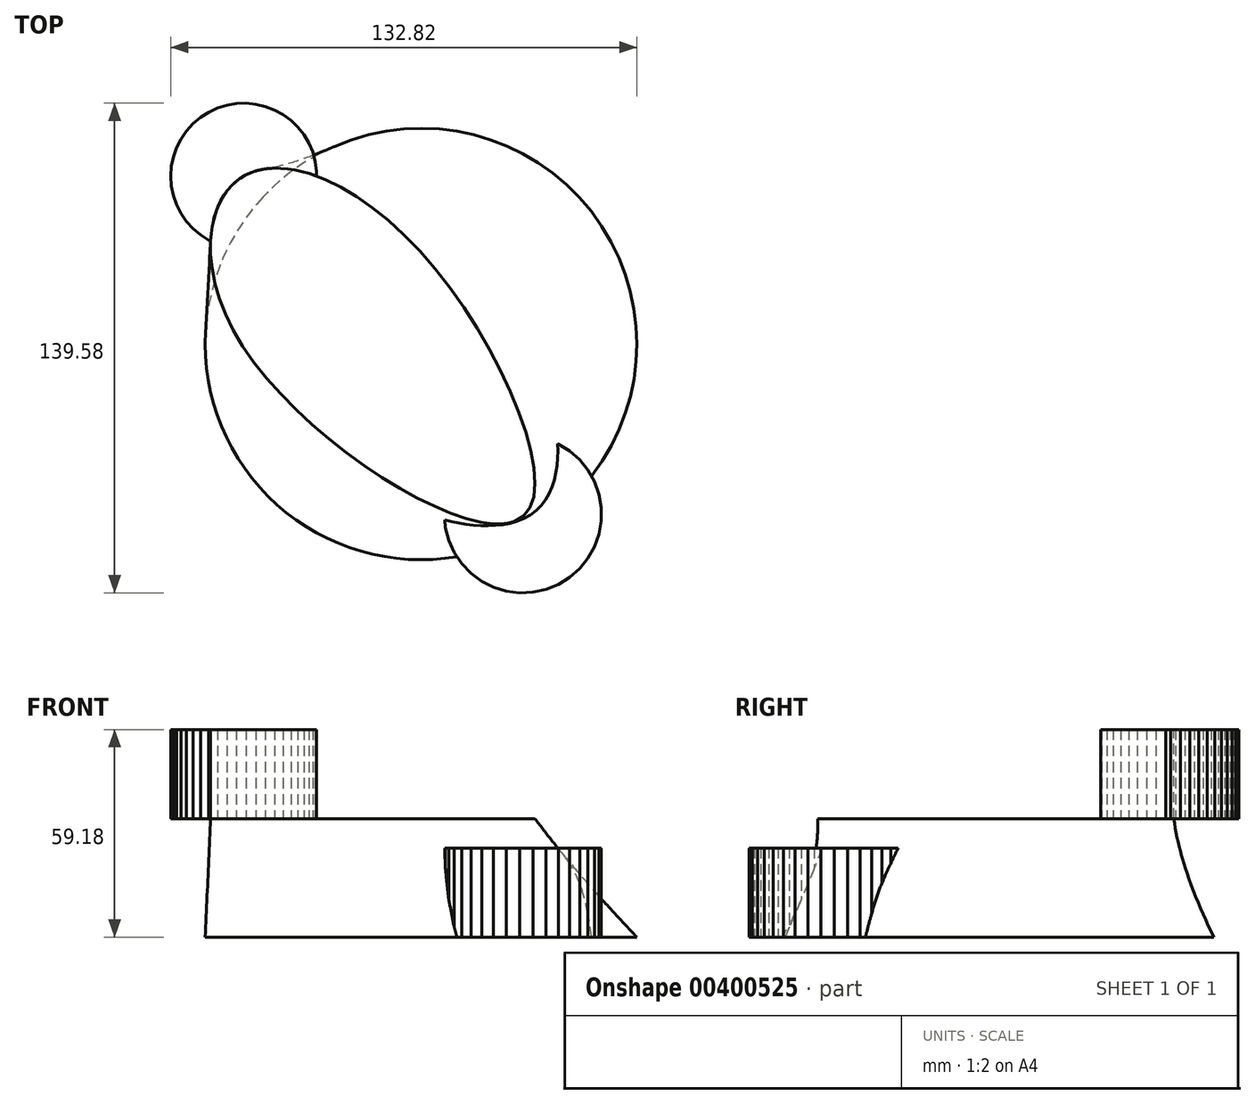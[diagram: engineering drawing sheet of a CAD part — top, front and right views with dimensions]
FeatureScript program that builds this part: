
annotation { "Feature Type Name" : "Feature", "Feature Type Description" : "" }
export const myFeature = defineFeature(function(context is Context, id is Id, definition is map)
    precondition{}
    {
        {
            var Q0;
            Q0=qCreatedBy(makeId("Top.planeOp"),FACE);
            cPlane(context, id + "F0", {"entities" : qUnion([Q0]), "cplaneType" : CPlaneType.OFFSET, "offset" : 33.78 * mm, "width" : 152.4 * mm, "height" : 152.4 * mm});
        }
        {
            var Q0;
            Q0=qCreatedBy(makeId("Top.planeOp"),FACE);
            var sketch = newSketch(context, id + "F1", { "sketchPlane" : qUnion([Q0])});
            skCircle(sketch, "E0", {"center": v(0, 0) * mm, "radius": 61.5 * mm});
            skSolve(sketch);
        }
        {
            var Q0;
            Q0=qCreatedBy(id+"F0.planeOp",FACE);
            var sketch = newSketch(context, id + "F2", { "sketchPlane" : qUnion([Q0])});
            skFitSpline(sketch, "E1", {"points": [v(-51.05, 47.53) * mm, v(0, 26.14) * mm, v(28.63, -49.58) * mm, v(-51.22, 0) * mm, v(-51.05, 47.53) * mm]});
            skSolve(sketch);
        }
        {
            var Q0;
            Q0 = qSketchRegion(id + "F2", true);
            var Q1;
            Q1 = qSketchRegion(id + "F1", true);
            loft(context, id + "F3", {"sheetProfilesArray" : [{ "sheetProfileEntities" : qUnion([Q0]) }, { "sheetProfileEntities" : qUnion([Q1]) }]});
        }
        {
            var Q0;
            Q0=makeQuery(id+"F3.opLoft","CAP_FACE",FACE,{"disambiguationData":[OSD([makeQuery(id+"F2.imprint","IMPRINT",FACE,{"disambiguationData":[TD([[makeQuery(id+"F2.imprint","IMPRINT",EDGE,{"derivedFrom":sQuery(id+"F2.wireOp",EDGE,"E1")}),-1.0]])]})])],"isStart":true});
            var sketch = newSketch(context, id + "F4", { "sketchPlane" : qUnion([Q0])});
            skCircle(sketch, "E2.cCircle", {"center": v(-50.5, 47.86) * mm, "radius": 20.76 * mm, "construction": true});
            skLineSegment(sketch, "E2.0", {"start": v(-29.74, 49.25) * mm, "end": v(-29.74, 46.47) * mm});
            skLineSegment(sketch, "E2.1", {"start": v(-29.74, 46.47) * mm, "end": v(-30.11, 43.71) * mm});
            skLineSegment(sketch, "E2.2", {"start": v(-30.11, 43.71) * mm, "end": v(-30.85, 41.03) * mm});
            skLineSegment(sketch, "E2.3", {"start": v(-30.85, 41.03) * mm, "end": v(-31.93, 38.47) * mm});
            skLineSegment(sketch, "E2.4", {"start": v(-31.93, 38.47) * mm, "end": v(-33.35, 36.08) * mm});
            skLineSegment(sketch, "E2.5", {"start": v(-33.35, 36.08) * mm, "end": v(-35.07, 33.9) * mm});
            skLineSegment(sketch, "E2.6", {"start": v(-35.07, 33.9) * mm, "end": v(-37.07, 31.97) * mm});
            skLineSegment(sketch, "E2.7", {"start": v(-37.07, 31.97) * mm, "end": v(-39.3, 30.32) * mm});
            skLineSegment(sketch, "E2.8", {"start": v(-39.3, 30.32) * mm, "end": v(-41.75, 28.98) * mm});
            skLineSegment(sketch, "E2.9", {"start": v(-41.75, 28.98) * mm, "end": v(-44.34, 27.98) * mm});
            skLineSegment(sketch, "E2.10", {"start": v(-44.34, 27.98) * mm, "end": v(-47.04, 27.34) * mm});
            skLineSegment(sketch, "E2.11", {"start": v(-47.04, 27.34) * mm, "end": v(-49.8, 27.06) * mm});
            skLineSegment(sketch, "E2.12", {"start": v(-49.8, 27.06) * mm, "end": v(-52.59, 27.15) * mm});
            skLineSegment(sketch, "E2.13", {"start": v(-52.59, 27.15) * mm, "end": v(-55.33, 27.62) * mm});
            skLineSegment(sketch, "E2.14", {"start": v(-55.33, 27.62) * mm, "end": v(-57.98, 28.44) * mm});
            skLineSegment(sketch, "E2.15", {"start": v(-57.98, 28.44) * mm, "end": v(-60.5, 29.6) * mm});
            skLineSegment(sketch, "E2.16", {"start": v(-60.5, 29.6) * mm, "end": v(-62.85, 31.1) * mm});
            skLineSegment(sketch, "E2.17", {"start": v(-62.85, 31.1) * mm, "end": v(-64.97, 32.9) * mm});
            skLineSegment(sketch, "E2.18", {"start": v(-64.97, 32.9) * mm, "end": v(-66.84, 34.96) * mm});
            skLineSegment(sketch, "E2.19", {"start": v(-66.84, 34.96) * mm, "end": v(-68.4, 37.25) * mm});
            skLineSegment(sketch, "E2.20", {"start": v(-68.4, 37.25) * mm, "end": v(-69.66, 39.73) * mm});
            skLineSegment(sketch, "E2.21", {"start": v(-69.66, 39.73) * mm, "end": v(-70.57, 42.36) * mm});
            skLineSegment(sketch, "E2.22", {"start": v(-70.57, 42.36) * mm, "end": v(-71.13, 45.08) * mm});
            skLineSegment(sketch, "E2.23", {"start": v(-71.13, 45.08) * mm, "end": v(-71.31, 47.86) * mm});
            skLineSegment(sketch, "E2.24", {"start": v(-71.31, 47.86) * mm, "end": v(-71.13, 50.63) * mm});
            skLineSegment(sketch, "E2.25", {"start": v(-71.13, 50.63) * mm, "end": v(-70.57, 53.35) * mm});
            skLineSegment(sketch, "E2.26", {"start": v(-70.57, 53.35) * mm, "end": v(-69.66, 55.98) * mm});
            skLineSegment(sketch, "E2.27", {"start": v(-69.66, 55.98) * mm, "end": v(-68.4, 58.46) * mm});
            skLineSegment(sketch, "E2.28", {"start": v(-68.4, 58.46) * mm, "end": v(-66.84, 60.75) * mm});
            skLineSegment(sketch, "E2.29", {"start": v(-66.84, 60.75) * mm, "end": v(-64.97, 62.81) * mm});
            skLineSegment(sketch, "E2.30", {"start": v(-64.97, 62.81) * mm, "end": v(-62.85, 64.6) * mm});
            skLineSegment(sketch, "E2.31", {"start": v(-62.85, 64.6) * mm, "end": v(-60.5, 66.1) * mm});
            skLineSegment(sketch, "E2.32", {"start": v(-60.5, 66.1) * mm, "end": v(-57.98, 67.28) * mm});
            skLineSegment(sketch, "E2.33", {"start": v(-57.98, 67.28) * mm, "end": v(-55.33, 68.1) * mm});
            skLineSegment(sketch, "E2.34", {"start": v(-55.33, 68.1) * mm, "end": v(-52.59, 68.56) * mm});
            skLineSegment(sketch, "E2.35", {"start": v(-52.59, 68.56) * mm, "end": v(-49.8, 68.65) * mm});
            skLineSegment(sketch, "E2.36", {"start": v(-49.8, 68.65) * mm, "end": v(-47.04, 68.38) * mm});
            skLineSegment(sketch, "E2.37", {"start": v(-47.04, 68.38) * mm, "end": v(-44.34, 67.73) * mm});
            skLineSegment(sketch, "E2.38", {"start": v(-44.34, 67.73) * mm, "end": v(-41.75, 66.73) * mm});
            skLineSegment(sketch, "E2.39", {"start": v(-41.75, 66.73) * mm, "end": v(-39.3, 65.4) * mm});
            skLineSegment(sketch, "E2.40", {"start": v(-39.3, 65.4) * mm, "end": v(-37.07, 63.75) * mm});
            skLineSegment(sketch, "E2.41", {"start": v(-37.07, 63.75) * mm, "end": v(-35.07, 61.82) * mm});
            skLineSegment(sketch, "E2.42", {"start": v(-35.07, 61.82) * mm, "end": v(-33.35, 59.63) * mm});
            skLineSegment(sketch, "E2.43", {"start": v(-33.35, 59.63) * mm, "end": v(-31.93, 57.24) * mm});
            skLineSegment(sketch, "E2.44", {"start": v(-31.93, 57.24) * mm, "end": v(-30.85, 54.68) * mm});
            skLineSegment(sketch, "E2.45", {"start": v(-30.85, 54.68) * mm, "end": v(-30.11, 52) * mm});
            skLineSegment(sketch, "E2.46", {"start": v(-30.11, 52) * mm, "end": v(-29.74, 49.25) * mm});
            skPoint(sketch, "E2.0.midPoint", {"position": v(-29.74, 47.86) * mm});
            skSolve(sketch);
        }
        {
            var Q0;
            {var subQ0=sQuery(id+"F4.wireOp",EDGE,"E2.16");Q0=makeQuery(id+"F4.imprint","IMPRINT",FACE,{"disambiguationData":[TD([[makeQuery(id+"F4.imprint","IMPRINT",EDGE,{"derivedFrom":subQ0}),-1.0]])]});}
            extrude(context, id + "F5", {"entities" : qUnion([Q0]), "depth" : 25.4 * mm});
        }
        {
            var Q0;
            Q0=qCreatedBy(makeId("Top.planeOp"),FACE);
            var sketch = newSketch(context, id + "F6", { "sketchPlane" : qUnion([Q0])});
            skCircle(sketch, "E3.cCircle", {"center": v(29.04, -48.53) * mm, "radius": 22.34 * mm, "construction": true});
            skLineSegment(sketch, "E3.0", {"start": v(51.38, -46.63) * mm, "end": v(51.38, -50.44) * mm});
            skLineSegment(sketch, "E3.1", {"start": v(51.38, -50.44) * mm, "end": v(50.73, -54.18) * mm});
            skLineSegment(sketch, "E3.2", {"start": v(50.73, -54.18) * mm, "end": v(49.47, -57.77) * mm});
            skLineSegment(sketch, "E3.3", {"start": v(49.47, -57.77) * mm, "end": v(47.61, -61.09) * mm});
            skLineSegment(sketch, "E3.4", {"start": v(47.61, -61.09) * mm, "end": v(45.22, -64.05) * mm});
            skLineSegment(sketch, "E3.5", {"start": v(45.22, -64.05) * mm, "end": v(42.37, -66.56) * mm});
            skLineSegment(sketch, "E3.6", {"start": v(42.37, -66.56) * mm, "end": v(39.13, -68.55) * mm});
            skLineSegment(sketch, "E3.7", {"start": v(39.13, -68.55) * mm, "end": v(35.6, -69.97) * mm});
            skLineSegment(sketch, "E3.8", {"start": v(35.6, -69.97) * mm, "end": v(31.89, -70.77) * mm});
            skLineSegment(sketch, "E3.9", {"start": v(31.89, -70.77) * mm, "end": v(28.09, -70.93) * mm});
            skLineSegment(sketch, "E3.10", {"start": v(28.09, -70.93) * mm, "end": v(24.32, -70.45) * mm});
            skLineSegment(sketch, "E3.11", {"start": v(24.32, -70.45) * mm, "end": v(20.68, -69.34) * mm});
            skLineSegment(sketch, "E3.12", {"start": v(20.68, -69.34) * mm, "end": v(17.28, -67.62) * mm});
            skLineSegment(sketch, "E3.13", {"start": v(17.28, -67.62) * mm, "end": v(14.23, -65.36) * mm});
            skLineSegment(sketch, "E3.14", {"start": v(14.23, -65.36) * mm, "end": v(11.6, -62.62) * mm});
            skLineSegment(sketch, "E3.15", {"start": v(11.6, -62.62) * mm, "end": v(9.47, -59.47) * mm});
            skLineSegment(sketch, "E3.16", {"start": v(9.47, -59.47) * mm, "end": v(7.9, -56) * mm});
            skLineSegment(sketch, "E3.17", {"start": v(7.9, -56) * mm, "end": v(6.94, -52.32) * mm});
            skLineSegment(sketch, "E3.18", {"start": v(6.94, -52.32) * mm, "end": v(6.62, -48.53) * mm});
            skLineSegment(sketch, "E3.19", {"start": v(6.62, -48.53) * mm, "end": v(6.94, -44.75) * mm});
            skLineSegment(sketch, "E3.20", {"start": v(6.94, -44.75) * mm, "end": v(7.9, -41.07) * mm});
            skLineSegment(sketch, "E3.21", {"start": v(7.9, -41.07) * mm, "end": v(9.47, -37.6) * mm});
            skLineSegment(sketch, "E3.22", {"start": v(9.47, -37.6) * mm, "end": v(11.6, -34.45) * mm});
            skLineSegment(sketch, "E3.23", {"start": v(11.6, -34.45) * mm, "end": v(14.23, -31.7) * mm});
            skLineSegment(sketch, "E3.24", {"start": v(14.23, -31.7) * mm, "end": v(17.28, -29.44) * mm});
            skLineSegment(sketch, "E3.25", {"start": v(17.28, -29.44) * mm, "end": v(20.68, -27.73) * mm});
            skLineSegment(sketch, "E3.26", {"start": v(20.68, -27.73) * mm, "end": v(24.32, -26.62) * mm});
            skLineSegment(sketch, "E3.27", {"start": v(24.32, -26.62) * mm, "end": v(28.09, -26.14) * mm});
            skLineSegment(sketch, "E3.28", {"start": v(28.09, -26.14) * mm, "end": v(31.89, -26.3) * mm});
            skLineSegment(sketch, "E3.29", {"start": v(31.89, -26.3) * mm, "end": v(35.6, -27.1) * mm});
            skLineSegment(sketch, "E3.30", {"start": v(35.6, -27.1) * mm, "end": v(39.13, -28.52) * mm});
            skLineSegment(sketch, "E3.31", {"start": v(39.13, -28.52) * mm, "end": v(42.37, -30.5) * mm});
            skLineSegment(sketch, "E3.32", {"start": v(42.37, -30.5) * mm, "end": v(45.22, -33.02) * mm});
            skLineSegment(sketch, "E3.33", {"start": v(45.22, -33.02) * mm, "end": v(47.61, -35.98) * mm});
            skLineSegment(sketch, "E3.34", {"start": v(47.61, -35.98) * mm, "end": v(49.47, -39.3) * mm});
            skLineSegment(sketch, "E3.35", {"start": v(49.47, -39.3) * mm, "end": v(50.73, -42.88) * mm});
            skLineSegment(sketch, "E3.36", {"start": v(50.73, -42.88) * mm, "end": v(51.38, -46.63) * mm});
            skPoint(sketch, "E3.0.midPoint", {"position": v(51.38, -48.53) * mm});
            skSolve(sketch);
        }
        {
            var Q0;
            Q0=makeQuery(id+"F6.imprint","IMPRINT",FACE,{"disambiguationData":[TD([[makeQuery(id+"F6.imprint","IMPRINT",EDGE,{"derivedFrom":sQuery(id+"F6.wireOp",EDGE,"E3.0")}),-1.0]])]});
            extrude(context, id + "F7", {"entities" : qUnion([Q0]), "operationType" : NewBodyOperationType.ADD, "depth" : 25.4 * mm});
        }
    });
